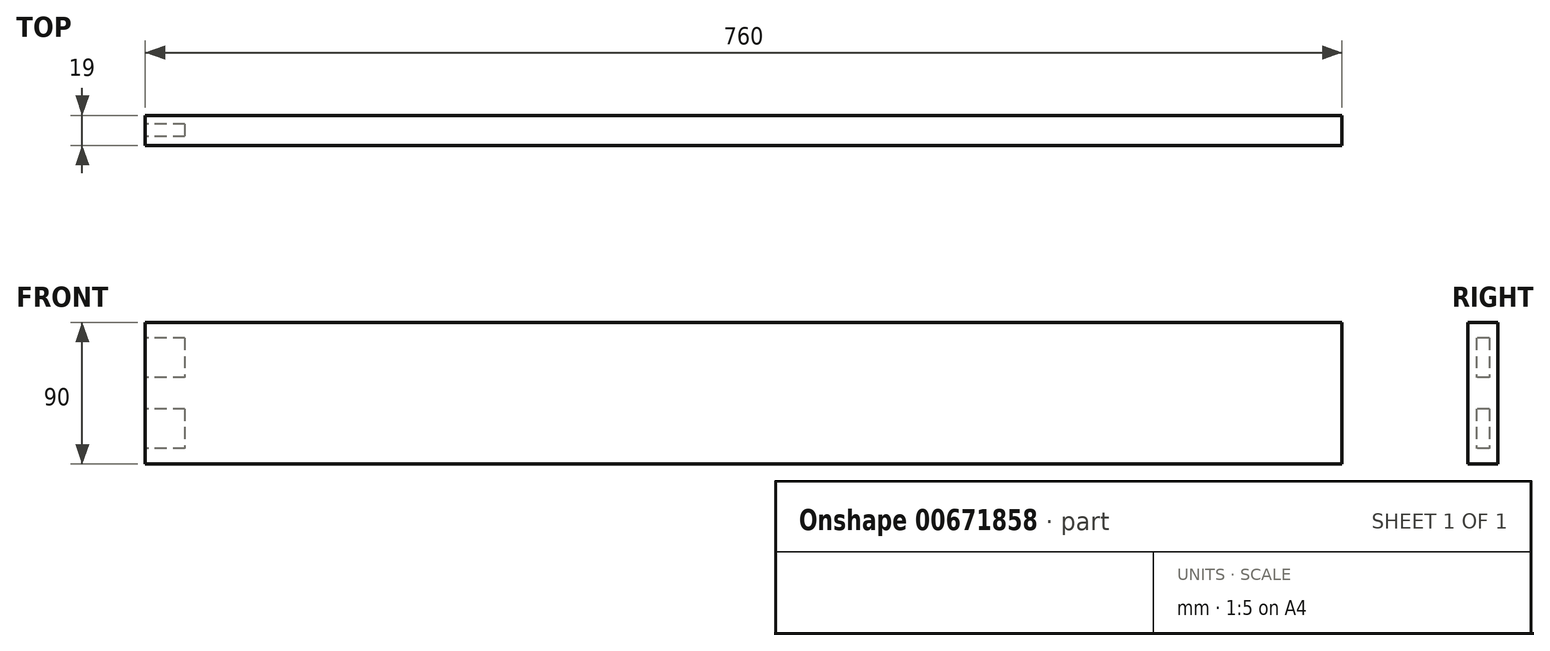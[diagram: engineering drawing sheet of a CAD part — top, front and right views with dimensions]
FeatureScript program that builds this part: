
annotation { "Feature Type Name" : "Feature", "Feature Type Description" : "" }
export const myFeature = defineFeature(function(context is Context, id is Id, definition is map)
    precondition{}
    {
        {
            var Q0;
            Q0=qCreatedBy(makeId("Front.planeOp"),FACE);
            var sketch = newSketch(context, id + "F0", { "sketchPlane" : qUnion([Q0])});
            skLineSegment(sketch, "E0.bottom", {"start": v(380, -45) * mm, "end": v(-380, -45) * mm});
            skLineSegment(sketch, "E0.top", {"start": v(380, 45) * mm, "end": v(-380, 45) * mm});
            skLineSegment(sketch, "E0.left", {"start": v(380, -45) * mm, "end": v(380, 45) * mm});
            skLineSegment(sketch, "E0.right", {"start": v(-380, -45) * mm, "end": v(-380, 45) * mm});
            skPoint(sketch, "E0.middle", {"position": v(0, 0) * mm});
            skSolve(sketch);
        }
        {
            var Q0;
            Q0=makeQuery(id+"F0.imprint","IMPRINT",FACE,{"disambiguationData":[TD([[makeQuery(id+"F0.imprint","IMPRINT",EDGE,{"derivedFrom":sQuery(id+"F0.wireOp",EDGE,"E0.bottom")}),-1.0]])]});
            extrude(context, id + "F1", {"entities" : qUnion([Q0]), "depth" : 19 * mm, "offsetDistance" : 25 * mm});
        }
        {
            var Q0;
            Q0=makeQuery(id+"F1.opExtrude","SWEPT_FACE",FACE,{"disambiguationData":[OSD([sQuery(id+"F0.wireOp",EDGE,"E0.right")])]});
            var sketch = newSketch(context, id + "F2", { "sketchPlane" : qUnion([Q0])});
            skLineSegment(sketch, "E1.bottom", {"start": v(5.5, 35) * mm, "end": v(13.5, 35) * mm});
            skLineSegment(sketch, "E1.top", {"start": v(5.5, 10) * mm, "end": v(13.5, 10) * mm});
            skLineSegment(sketch, "E1.left", {"start": v(5.5, 35) * mm, "end": v(5.5, 10) * mm});
            skLineSegment(sketch, "E1.right", {"start": v(13.5, 35) * mm, "end": v(13.5, 10) * mm});
            skLineSegment(sketch, "E2.bottom", {"start": v(5.5, -10) * mm, "end": v(13.5, -10) * mm});
            skLineSegment(sketch, "E2.top", {"start": v(5.5, -35) * mm, "end": v(13.5, -35) * mm});
            skLineSegment(sketch, "E2.left", {"start": v(5.5, -10) * mm, "end": v(5.5, -35) * mm});
            skLineSegment(sketch, "E2.right", {"start": v(13.5, -10) * mm, "end": v(13.5, -35) * mm});
            skSolve(sketch);
        }
        {
            var Q0;
            Q0=makeQuery(id+"F2.imprint","IMPRINT",FACE,{"disambiguationData":[TD([[makeQuery(id+"F2.imprint","IMPRINT",EDGE,{"derivedFrom":sQuery(id+"F2.wireOp",EDGE,"E1.bottom")}),-1.0]])]});
            var Q1;
            Q1=makeQuery(id+"F2.imprint","IMPRINT",FACE,{"disambiguationData":[TD([[makeQuery(id+"F2.imprint","IMPRINT",EDGE,{"derivedFrom":sQuery(id+"F2.wireOp",EDGE,"E2.bottom")}),-1.0]])]});
            extrude(context, id + "F3", {"entities" : qUnion([Q0, Q1]), "operationType" : NewBodyOperationType.REMOVE, "oppositeDirection" : true, "depth" : 25 * mm, "offsetDistance" : 25 * mm});
        }
    });
